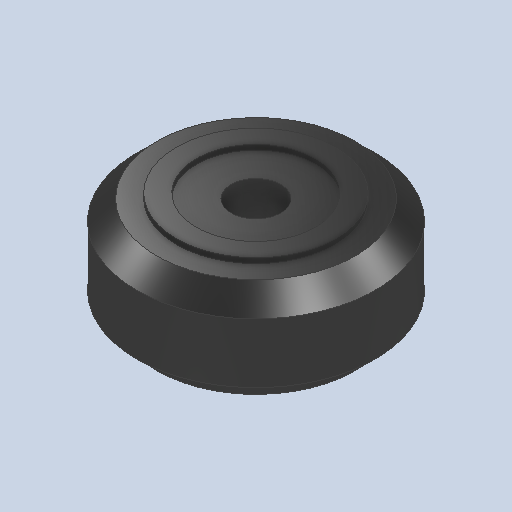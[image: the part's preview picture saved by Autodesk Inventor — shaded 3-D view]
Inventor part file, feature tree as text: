
AUTODESK INVENTOR PART (.ipt)
format: ipt  version: 2023 (Build 270158000, 158)  size: 149,504 bytes
history: native  units: mm
features: mirror x1
ambient origin geometry x8: Origin, YZ Plane, XZ Plane, XY Plane, X Axis, Y Axis, Z Axis, Center Point
bodies: Solid1 (feature_tree)
feature tree (1):
  mirror  "Mirror1"
